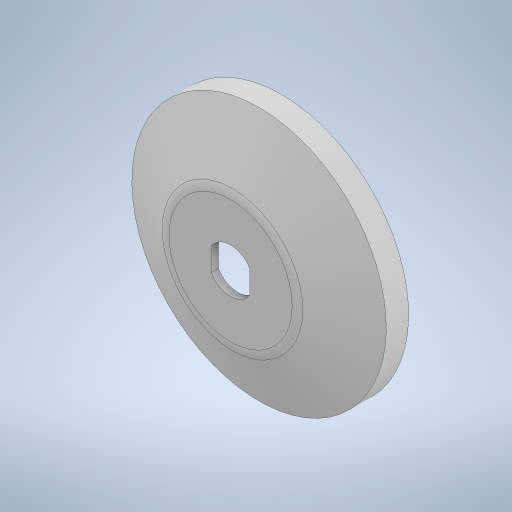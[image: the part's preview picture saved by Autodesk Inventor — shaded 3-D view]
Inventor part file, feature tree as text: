
AUTODESK INVENTOR PART (.ipt)
format: ipt  version: 2023 (Build 270158000, 158)  size: 287,744 bytes
history: native  units: mm
features: sketch x4, extrude x3, revolve x1, fillet x1, plane x1, pattern_circular x1
ambient origin geometry x8: Origin, YZ Plane, XZ Plane, XY Plane, X Axis, Y Axis, Z Axis, Center Point
bodies: Solid1 (feature_tree)
feature tree (11):
  extrude  "Extrusion1"  Depth=19.0mm
  revolve  "Revolution1"  [1 undecoded]
  fillet  "Fillet1"  Radius=7.0mm
  plane  "Work Plane2"
  extrude  "Extrusion2"  Depth=11.0mm
  sketch  "Sketch4"  dims[d11=30.0mm d12=90.0deg d13=10.0mm d14=9.0mm d19=61.0mm d20=6.0mm d21=0.0mm d22=1.0mm d23=0.0mm d24=0.0mm d25=45.0mm d26=18.0mm d27=100.0mm d28=360.0deg]
  extrude  "Extrusion3"  TaperAngle=90.0deg  [1 undecoded]
  pattern_circular  "Circular Pattern1"  [2 undecoded]
  sketch  "Sketch1"  dims[d0=22.0mm d1=19.0mm]
  sketch  "Sketch2"  dims[d2=65.0mm d3=3.5mm d4=0.0mm d8=7.0mm]
  sketch  "Sketch3"  dims[d9=25.0mm d10=11.0mm]
note: 4 required parameter values undecoded (feature->parameter linkage not recoverable at this tier; creation-order binding heuristic only, values carry confidence <= 0.55)